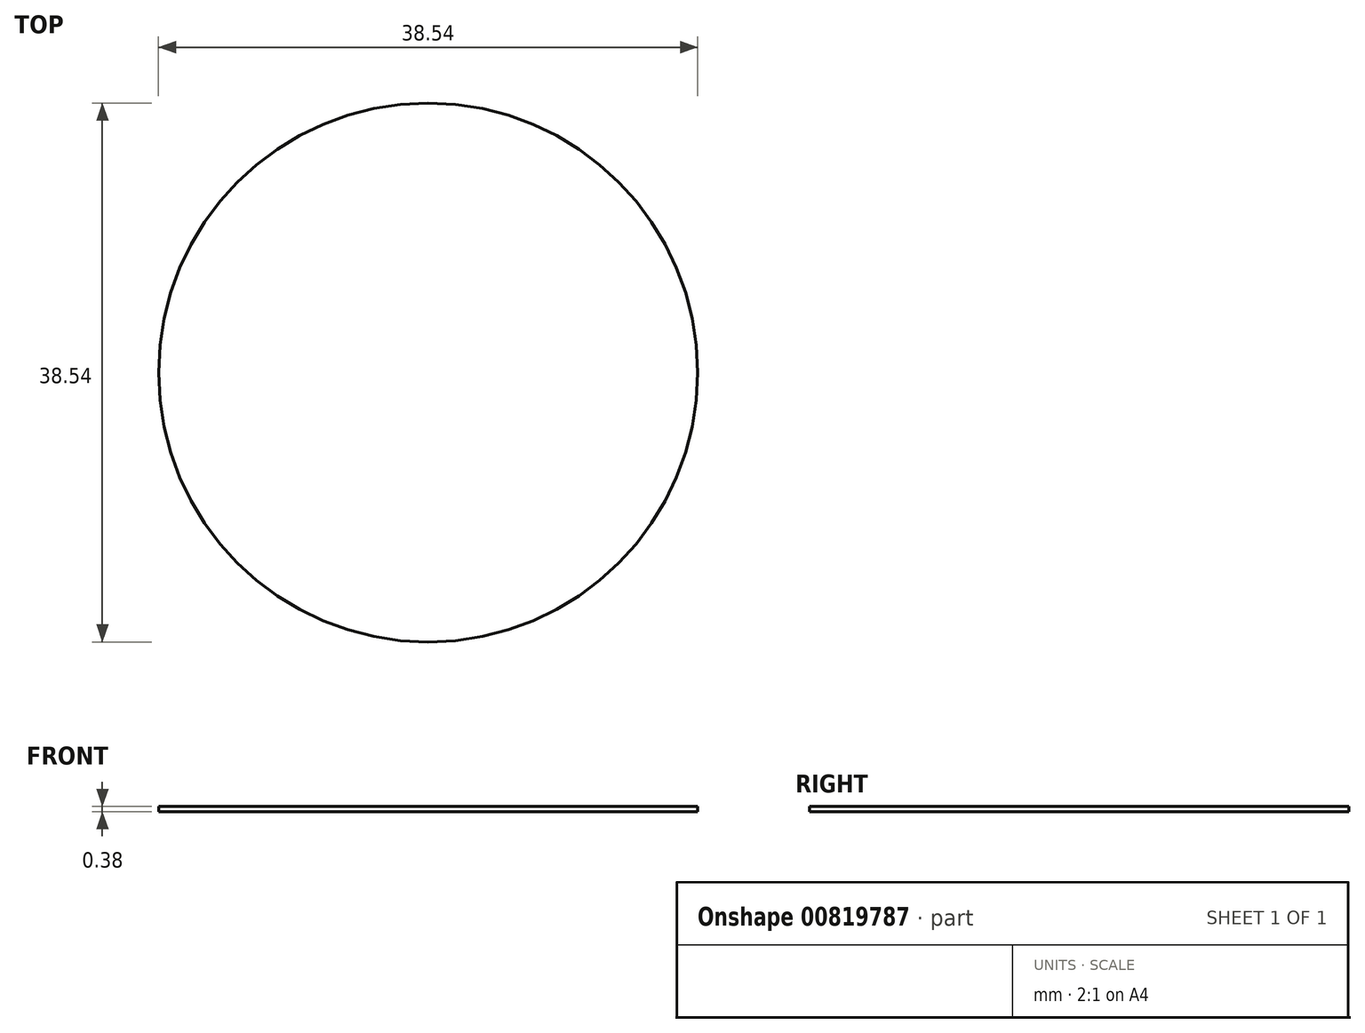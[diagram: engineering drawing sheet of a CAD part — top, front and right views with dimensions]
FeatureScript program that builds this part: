
annotation { "Feature Type Name" : "Feature", "Feature Type Description" : "" }
export const myFeature = defineFeature(function(context is Context, id is Id, definition is map)
    precondition{}
    {
        {
            var Q0;
            Q0=qCreatedBy(makeId("Top.planeOp"),FACE);
            var sketch = newSketch(context, id + "F0", { "sketchPlane" : qUnion([Q0])});
            skCircle(sketch, "E0", {"center": v(0, 0) * mm, "radius": 19.27 * mm});
            skSolve(sketch);
        }
        {
            var Q0;
            Q0 = qSketchRegion(id + "F0", true);
            extrude(context, id + "F1", {"entities" : qUnion([Q0]), "depth" : 0.38 * mm, "offsetDistance" : 25.4 * mm});
        }
    });
